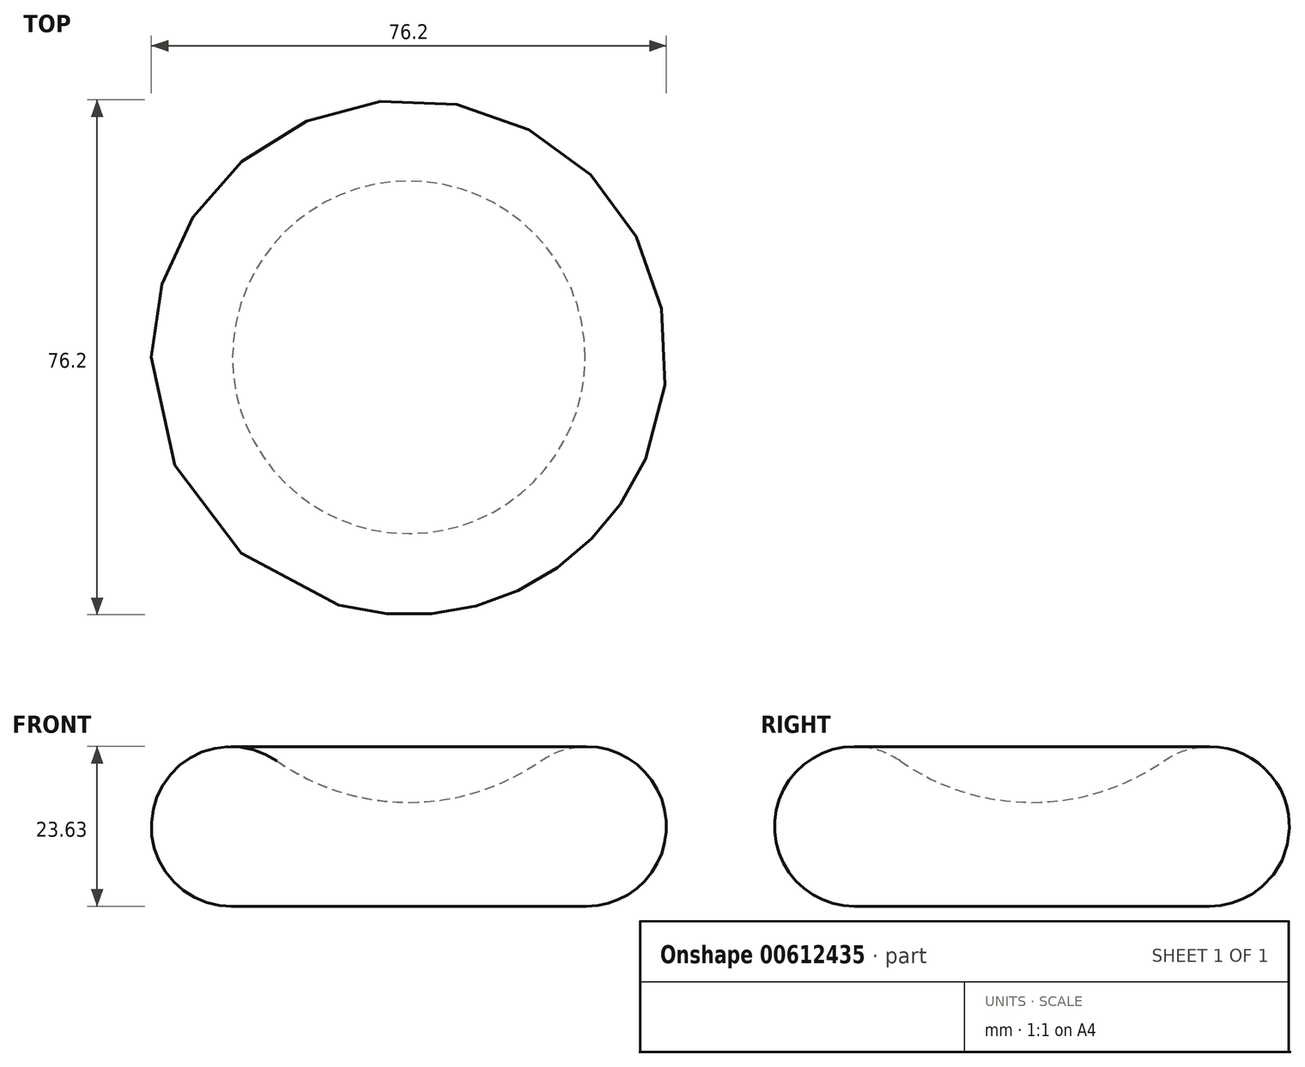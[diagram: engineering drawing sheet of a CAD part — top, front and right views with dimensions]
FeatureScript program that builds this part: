
annotation { "Feature Type Name" : "Feature", "Feature Type Description" : "" }
export const myFeature = defineFeature(function(context is Context, id is Id, definition is map)
    precondition{}
    {
        {
            var Q0;
            Q0=qCreatedBy(makeId("Front.planeOp"),FACE);
            var sketch = newSketch(context, id + "F0", { "sketchPlane" : qUnion([Q0])});
            skArc(sketch, "E0", {"start": v(-19.53, 21.5) * mm, "mid": v(-37.59, 15.26) * mm, "end": v(-26.09, 0) * mm});
            skArc(sketch, "E1", {"start": v(-19.53, 21.5) * mm, "mid": v(-10.23, 16.94) * mm, "end": v(0, 15.37) * mm});
            skLineSegment(sketch, "E2", {"start": v(-26.09, 0) * mm, "end": v(0, 0) * mm});
            skLineSegment(sketch, "E3", {"start": v(0, 0) * mm, "end": v(0, 15.37) * mm});
            skSolve(sketch);
        }
        {
            var Q0;
            Q0=makeQuery(id+"F0.imprint","IMPRINT",FACE,{"disambiguationData":[TD([[makeQuery(id+"F0.imprint","IMPRINT",EDGE,{"derivedFrom":sQuery(id+"F0.wireOp",EDGE,"E0")}),1.0]])]});
            var Q1;
            Q1=sQuery(id+"F0.wireOp",EDGE,"E3");
            revolve(context, id + "F1", {"entities" : qUnion([Q0]), "axis" : qUnion([Q1]), "revolveType" : RevolveType.FULL});
        }
        {
            var Q0;
            Q0=qCreatedBy(makeId("Top.planeOp"),FACE);
            cPlane(context, id + "F2", {"entities" : qUnion([Q0]), "cplaneType" : CPlaneType.OFFSET, "offset" : 25.4 * mm, "width" : 152.4 * mm, "height" : 152.4 * mm});
        }
    });
